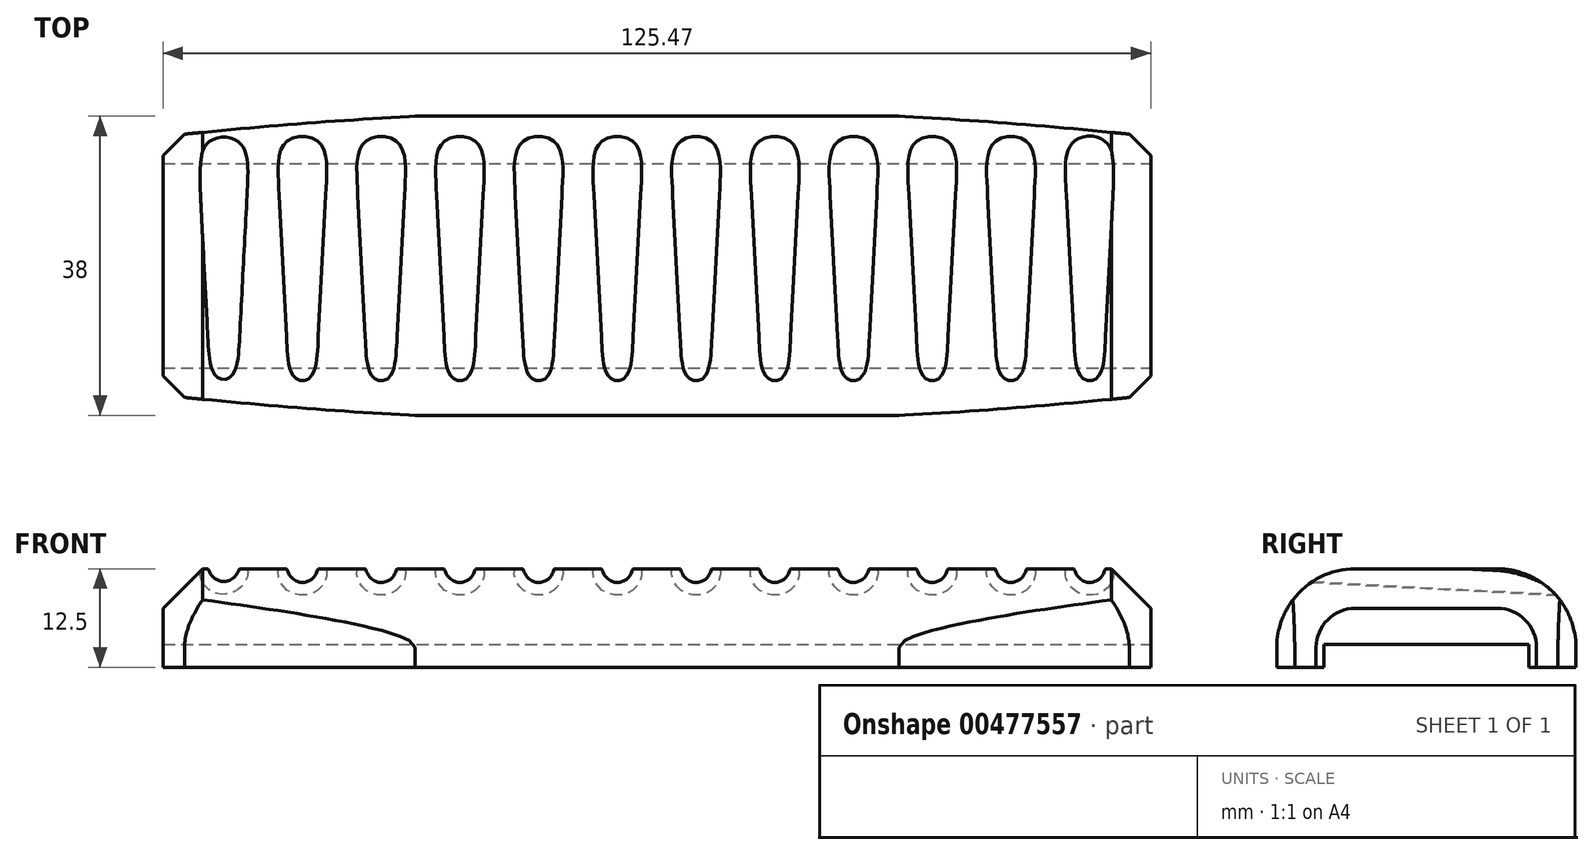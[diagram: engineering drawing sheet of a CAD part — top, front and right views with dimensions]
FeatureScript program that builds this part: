
annotation { "Feature Type Name" : "Feature", "Feature Type Description" : "" }
export const myFeature = defineFeature(function(context is Context, id is Id, definition is map)
    precondition{}
    {
        {
            var Q0;
            Q0=qCreatedBy(makeId("Top.planeOp"),FACE);
            var sketch = newSketch(context, id + "F0", { "sketchPlane" : qUnion([Q0])});
            skLineSegment(sketch, "E0", {"start": v(-42.43, 0) * mm, "end": v(-42.43, 38) * mm});
            skLineSegment(sketch, "E1", {"start": v(-42.43, 38) * mm, "end": v(83.04, 38) * mm});
            skLineSegment(sketch, "E2", {"start": v(83.04, 38) * mm, "end": v(83.04, 0) * mm});
            skLineSegment(sketch, "E3", {"start": v(83.04, 0) * mm, "end": v(-42.43, 0) * mm});
            skSolve(sketch);
        }
        {
            var Q0;
            Q0 = qSketchRegion(id + "F0", true);
            extrude(context, id + "F1", {"entities" : qUnion([Q0]), "depth" : 12.5 * mm});
        }
        {
            var Q0;
            Q0=qCreatedBy(makeId("Right.planeOp"),FACE);
            var sketch = newSketch(context, id + "F2", { "sketchPlane" : qUnion([Q0])});
            skLineSegment(sketch, "E4", {"start": v(32, 0) * mm, "end": v(32, 2.9) * mm});
            skLineSegment(sketch, "E5", {"start": v(32, 2.9) * mm, "end": v(6, 2.9) * mm});
            skLineSegment(sketch, "E6", {"start": v(6, 2.9) * mm, "end": v(6, 0) * mm});
            skLineSegment(sketch, "E7", {"start": v(32, 0) * mm, "end": v(6, 0) * mm});
            skSolve(sketch);
        }
        {
            var Q0;
            Q0 = qSketchRegion(id + "F2", true);
            extrude(context, id + "F3", {"entities" : qUnion([Q0]), "operationType" : NewBodyOperationType.REMOVE, "endBound" : BoundingType.SYMMETRIC, "oppositeDirection" : true, "depth" : 196.8 * mm});
        }
        {
            var Q0;
            Q0=makeQuery(id+"F1.opExtrude","CAP_EDGE",EDGE,{"disambiguationData":[OSD([sQuery(id+"F0.wireOp",EDGE,"E1")])],"isStart":false});
            var Q1;
            Q1=makeQuery(id+"F1.opExtrude","CAP_EDGE",EDGE,{"disambiguationData":[OSD([sQuery(id+"F0.wireOp",EDGE,"E3")])],"isStart":false});
            fillet(context, id + "F4", {"entities" : qUnion([Q0, Q1]), "radius" : 10 * mm, "tangentPropagation" : true, "allowEdgeOverflow" : false});
        }
        {
            var Q0;
            Q0=qCreatedBy(makeId("Front.planeOp"),FACE);
            var sketch = newSketch(context, id + "F5", { "sketchPlane" : qUnion([Q0])});
            skCircle(sketch, "E8", {"center": v(-34.73, 12.63) * mm, "radius": 1.5 * mm});
            skCircle(sketch, "E9", {"center": v(-24.73, 12.5) * mm, "radius": 1.5 * mm});
            skCircle(sketch, "E10", {"center": v(-14.73, 12.5) * mm, "radius": 1.5 * mm});
            skCircle(sketch, "E11", {"center": v(-4.73, 12.5) * mm, "radius": 1.5 * mm});
            skCircle(sketch, "E12", {"center": v(5.27, 12.5) * mm, "radius": 1.5 * mm});
            skCircle(sketch, "E13", {"center": v(15.27, 12.5) * mm, "radius": 1.5 * mm});
            skCircle(sketch, "E14", {"center": v(25.27, 12.5) * mm, "radius": 1.5 * mm});
            skCircle(sketch, "E15", {"center": v(35.27, 12.5) * mm, "radius": 1.5 * mm});
            skCircle(sketch, "E16", {"center": v(45.27, 12.5) * mm, "radius": 1.5 * mm});
            skCircle(sketch, "E17", {"center": v(55.27, 12.5) * mm, "radius": 1.5 * mm});
            skCircle(sketch, "E18", {"center": v(65.27, 12.5) * mm, "radius": 1.5 * mm});
            skCircle(sketch, "E19", {"center": v(75.27, 12.5) * mm, "radius": 1.5 * mm});
            skSolve(sketch);
        }
        {
            var Q0;
            Q0 = qSketchRegion(id + "F5", true);
            extrude(context, id + "F6", {"entities" : qUnion([Q0]), "operationType" : NewBodyOperationType.REMOVE, "oppositeDirection" : true, "depth" : 42.5 * mm, "hasDraft" : true, "draftAngle" : 3 * degree});
        }
        {
            var Q0;
            Q0=makeQuery(id+"F1.opExtrude","SWEPT_EDGE",EDGE,{"disambiguationData":[OSD([sQuery(id+"F0.wireOp",EDGE,"E0"),sQuery(id+"F0.wireOp",EDGE,"E1")])]});
            var Q1;
            Q1=makeQuery(id+"F1.opExtrude","SWEPT_EDGE",EDGE,{"disambiguationData":[OSD([sQuery(id+"F0.wireOp",EDGE,"E1"),sQuery(id+"F0.wireOp",EDGE,"E2")])]});
            chamfer(context, id + "F7", {"entities" : qUnion([Q0, Q1]), "width" : 5 * mm, "tangentPropagation" : true});
        }
        {
            var Q0;
            Q0=qCreatedBy(makeId("Top.planeOp"),FACE);
            var sketch = newSketch(context, id + "F8", { "sketchPlane" : qUnion([Q0])});
            skLineSegment(sketch, "E20", {"start": v(-54.73, 48) * mm, "end": v(-54.73, -10) * mm});
            skLineSegment(sketch, "E21", {"start": v(-54.73, -10) * mm, "end": v(95.27, -10) * mm});
            skLineSegment(sketch, "E22", {"start": v(95.27, -10) * mm, "end": v(95.27, 48) * mm});
            skLineSegment(sketch, "E23", {"start": v(95.27, 48) * mm, "end": v(-54.73, 48) * mm});
            skLineSegment(sketch, "E24", {"start": v(-46.43, 29) * mm, "end": v(-86.43, 29) * mm, "construction": true});
            skLineSegment(sketch, "E25", {"start": v(-46.43, 9) * mm, "end": v(-86.43, 9) * mm, "construction": true});
            skLineSegment(sketch, "E26", {"start": v(87.04, 29) * mm, "end": v(127.04, 29) * mm, "construction": true});
            skLineSegment(sketch, "E27", {"start": v(87.04, 9) * mm, "end": v(127.04, 9) * mm, "construction": true});
            skArc(sketch, "E28", {"start": v(127.04, 29) * mm, "mid": v(20.3, 38.8) * mm, "end": v(-86.43, 29) * mm});
            skArc(sketch, "E29", {"start": v(-86.43, 9) * mm, "mid": v(20.3, -0.8) * mm, "end": v(127.04, 9) * mm});
            skSolve(sketch);
        }
        {
            var Q0;
            {var subQ0=sQuery(id+"F0.wireOp",EDGE,"E1");var subQ1=sQuery(id+"F0.wireOp",EDGE,"E3");Q0=makeQuery(id+"F6.boolean.opBoolean","SPLIT",FACE,{"disambiguationData":[TD([makeQuery(id+"F4.opFillet","BLEND_FACE",FACE,{"disambiguationData":[OSD([subQ0])]}),makeQuery(id+"F4.opFillet","BLEND_FACE",FACE,{"disambiguationData":[OSD([subQ1])]}),makeQuery(id+"F6.opExtrude","SWEPT_FACE",FACE,{"disambiguationData":[OSD([sQuery(id+"F5.wireOp",EDGE,"E9")])]}),makeQuery(id+"F6.opExtrude","SWEPT_FACE",FACE,{"disambiguationData":[OSD([sQuery(id+"F5.wireOp",EDGE,"E10")])]})])],"derivedFrom":makeQuery(id+"F1.opExtrude","CAP_FACE",FACE,{"disambiguationData":[OSD([sQuery(id+"F0.wireOp",EDGE,"E0"),subQ0,sQuery(id+"F0.wireOp",EDGE,"E2"),subQ1])],"isStart":false})});}
            var Q1;
            {var subQ0=sQuery(id+"F8.wireOp",EDGE,"E23");Q1=makeQuery(id+"F8.imprint","IMPRINT",FACE,{"disambiguationData":[TD([[makeQuery(id+"F8.imprint","IMPRINT",EDGE,{"derivedFrom":subQ0}),1.0]])]});}
            var Q2;
            {var subQ0=sQuery(id+"F8.wireOp",EDGE,"E21");Q2=makeQuery(id+"F8.imprint","IMPRINT",FACE,{"disambiguationData":[TD([[makeQuery(id+"F8.imprint","IMPRINT",EDGE,{"derivedFrom":subQ0}),1.0]])]});}
            extrude(context, id + "F9", {"entities" : qUnion([Q0, Q1, Q2]), "operationType" : NewBodyOperationType.REMOVE, "depth" : 25 * mm});
        }
    });
